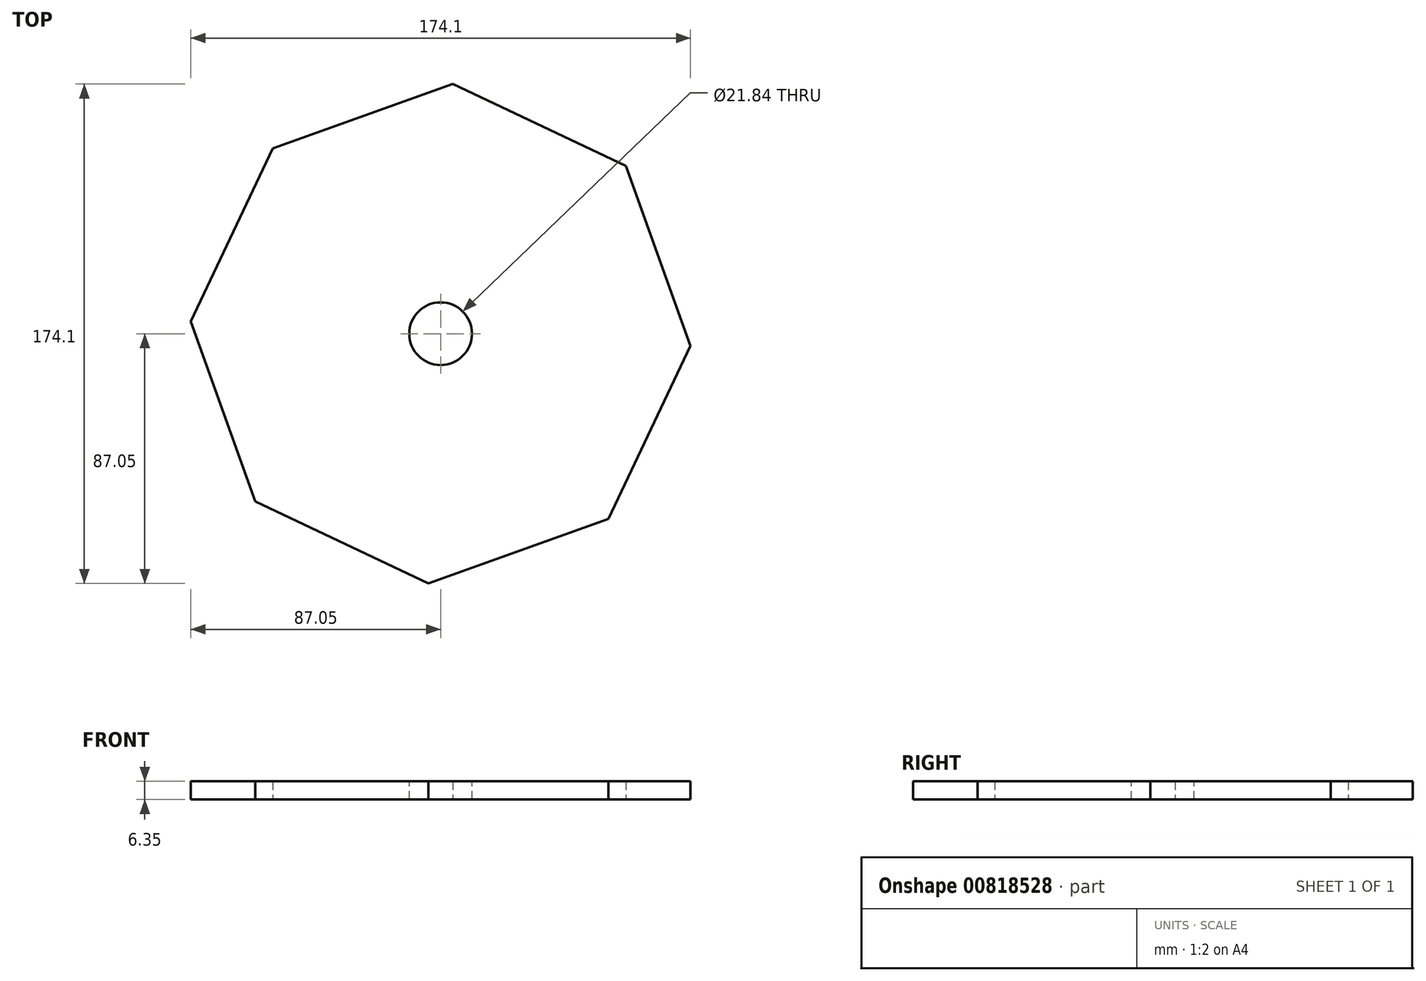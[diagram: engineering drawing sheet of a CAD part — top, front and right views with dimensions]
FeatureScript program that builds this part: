
annotation { "Feature Type Name" : "Feature", "Feature Type Description" : "" }
export const myFeature = defineFeature(function(context is Context, id is Id, definition is map)
    precondition{}
    {
        {
            var Q0;
            Q0=qCreatedBy(makeId("Top.planeOp"),FACE);
            var sketch = newSketch(context, id + "F0", { "sketchPlane" : qUnion([Q0])});
            skLineSegment(sketch, "E0.0", {"start": v(-87.05, 4.29) * mm, "end": v(-58.53, 64.59) * mm});
            skLineSegment(sketch, "E0.1", {"start": v(-58.53, 64.59) * mm, "end": v(4.29, 87.05) * mm});
            skLineSegment(sketch, "E0.2", {"start": v(4.29, 87.05) * mm, "end": v(64.59, 58.53) * mm});
            skLineSegment(sketch, "E0.3", {"start": v(64.59, 58.53) * mm, "end": v(87.05, -4.29) * mm});
            skLineSegment(sketch, "E0.4", {"start": v(87.05, -4.29) * mm, "end": v(58.53, -64.59) * mm});
            skLineSegment(sketch, "E0.5", {"start": v(58.53, -64.59) * mm, "end": v(-4.29, -87.05) * mm});
            skLineSegment(sketch, "E0.6", {"start": v(-4.29, -87.05) * mm, "end": v(-64.59, -58.53) * mm});
            skLineSegment(sketch, "E0.7", {"start": v(-64.59, -58.53) * mm, "end": v(-87.05, 4.29) * mm});
            skPoint(sketch, "E0.0.midPoint", {"position": v(-72.79, 34.44) * mm});
            skSolve(sketch);
        }
        {
            var Q0;
            Q0=makeQuery(id+"F0.imprint","IMPRINT",FACE,{"disambiguationData":[TD([[makeQuery(id+"F0.imprint","IMPRINT",EDGE,{"derivedFrom":sQuery(id+"F0.wireOp",EDGE,"E0.0")}),-1.0]])]});
            extrude(context, id + "F1", {"entities" : qUnion([Q0]), "depth" : 6.35 * mm, "offsetDistance" : 25.4 * mm});
        }
        {
            var Q0;
            Q0=makeQuery(id+"F1.opExtrude","CAP_FACE",FACE,{"disambiguationData":[OSD([sQuery(id+"F0.wireOp",EDGE,"E0.0"),sQuery(id+"F0.wireOp",EDGE,"E0.1"),sQuery(id+"F0.wireOp",EDGE,"E0.2"),sQuery(id+"F0.wireOp",EDGE,"E0.3"),sQuery(id+"F0.wireOp",EDGE,"E0.4"),sQuery(id+"F0.wireOp",EDGE,"E0.5"),sQuery(id+"F0.wireOp",EDGE,"E0.6"),sQuery(id+"F0.wireOp",EDGE,"E0.7")])],"isStart":false});
            var sketch = newSketch(context, id + "F2", { "sketchPlane" : qUnion([Q0])});
            skCircle(sketch, "E1", {"center": v(0, 0) * mm, "radius": 10.92 * mm});
            skSolve(sketch);
        }
        {
            var Q0;
            Q0 = qSketchRegion(id + "F2", true);
            extrude(context, id + "F3", {"entities" : qUnion([Q0]), "operationType" : NewBodyOperationType.REMOVE, "oppositeDirection" : true, "depth" : 25.4 * mm, "offsetDistance" : 25.4 * mm});
        }
    });
